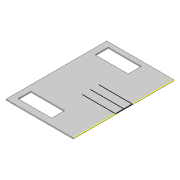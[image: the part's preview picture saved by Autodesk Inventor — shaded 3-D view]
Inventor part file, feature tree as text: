
AUTODESK INVENTOR PART (.ipt)
format: ipt  version: 2019 (Build 230136000, 136)  size: 100,864 bytes
history: native  units: in
note: dims shown in document units (in); Inventor stores cm internally (conversion verified against a paired STEP export)
features: sketch x4, extrude x2
ambient origin geometry x8: Origin, YZ Plane, XZ Plane, XY Plane, X Axis, Y Axis, Z Axis, Center Point
bodies: Solid1 (feature_tree)
feature tree (6):
  extrude  "Extrusion1"  Depth=0.1181in
  sketch  "Sketch2"  dims[d2=11.811in d3=0.0in d12=3.937in d13=0.0in]
  extrude  "Extrusion2"  Depth=3.937in TaperAngle=0.0deg
  sketch  "Sketch4"
  sketch  "Sketch1"  dims[d0=7.874in d1=0.1181in]
  sketch  "Sketch3"
